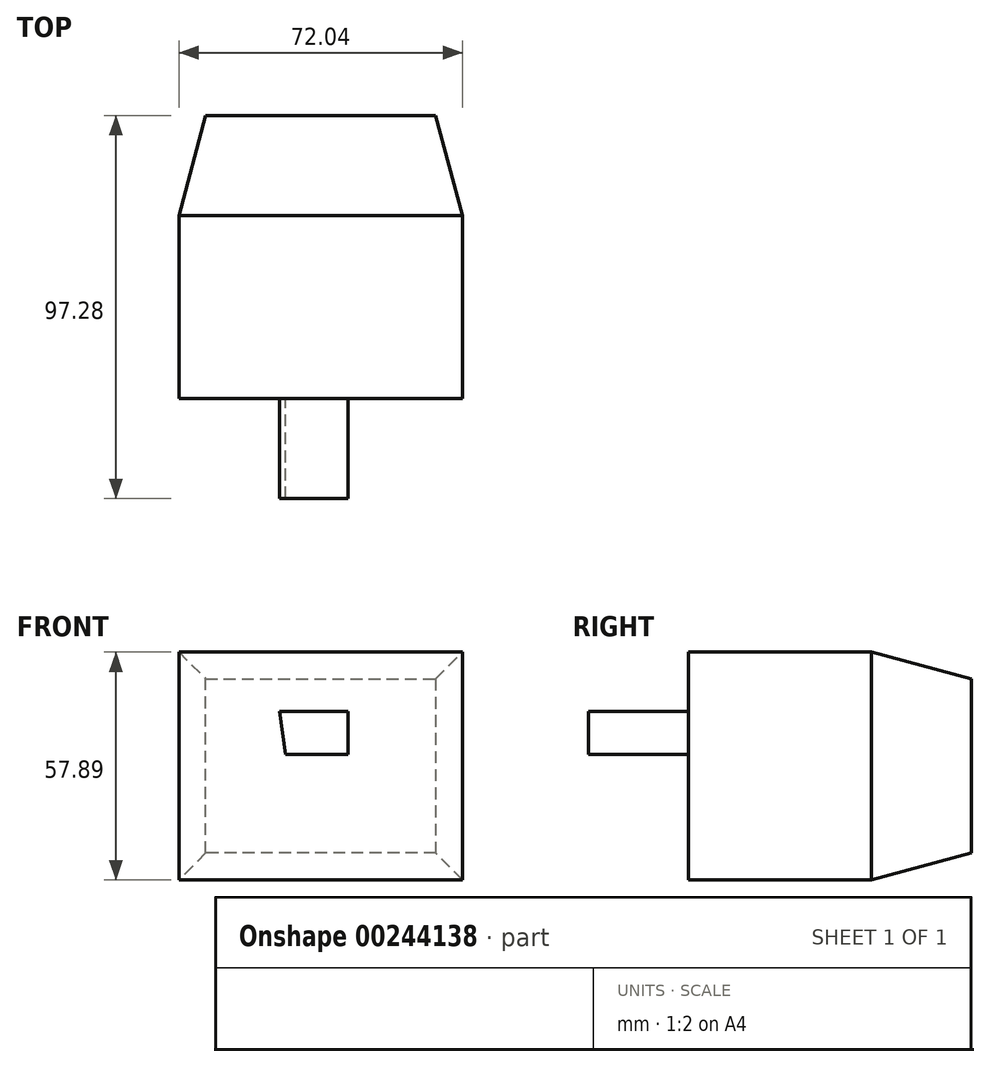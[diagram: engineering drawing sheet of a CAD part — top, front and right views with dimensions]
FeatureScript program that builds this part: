
annotation { "Feature Type Name" : "Feature", "Feature Type Description" : "" }
export const myFeature = defineFeature(function(context is Context, id is Id, definition is map)
    precondition{}
    {
        {
            var Q0;
            Q0=qCreatedBy(makeId("Front.planeOp"),FACE);
            var sketch = newSketch(context, id + "F0", { "sketchPlane" : qUnion([Q0])});
            skLineSegment(sketch, "E0.bottom", {"start": v(0, 0) * mm, "end": v(58.42, 0) * mm});
            skLineSegment(sketch, "E0.top", {"start": v(0, 44.27) * mm, "end": v(58.42, 44.27) * mm});
            skLineSegment(sketch, "E0.left", {"start": v(0, 0) * mm, "end": v(0, 44.27) * mm});
            skLineSegment(sketch, "E0.right", {"start": v(58.42, 0) * mm, "end": v(58.42, 44.27) * mm});
            skSolve(sketch);
        }
        {
            var Q0;
            Q0 = qSketchRegion(id + "F0", true);
            extrude(context, id + "F1", {"entities" : qUnion([Q0]), "depth" : 25.4 * mm, "hasDraft" : true, "draftAngle" : 15 * degree});
        }
        {
            var Q0;
            Q0=makeQuery(id+"F1.opExtrude","CAP_FACE",FACE,{"disambiguationData":[OSD([sQuery(id+"F0.wireOp",EDGE,"E0.bottom"),sQuery(id+"F0.wireOp",EDGE,"E0.top"),sQuery(id+"F0.wireOp",EDGE,"E0.left"),sQuery(id+"F0.wireOp",EDGE,"E0.right")])],"isStart":false});
            extrude(context, id + "F2", {"entities" : qUnion([Q0]), "operationType" : NewBodyOperationType.ADD, "depth" : 46.48 * mm, "offsetDistance" : 25.4 * mm});
        }
        {
            var Q0;
            Q0=makeQuery(id+"F2.opExtrude","CAP_FACE",FACE,{"disambiguationData":[OSD([sQuery(id+"F0.wireOp",EDGE,"E0.bottom"),sQuery(id+"F0.wireOp",EDGE,"E0.top"),sQuery(id+"F0.wireOp",EDGE,"E0.left"),sQuery(id+"F0.wireOp",EDGE,"E0.right")])],"isStart":false});
            var sketch = newSketch(context, id + "F3", { "sketchPlane" : qUnion([Q0])});
            skLineSegment(sketch, "E1", {"start": v(20.3, 25.1) * mm, "end": v(36.17, 25.1) * mm});
            skLineSegment(sketch, "E2", {"start": v(36.17, 25.1) * mm, "end": v(36.17, 36) * mm});
            skLineSegment(sketch, "E3", {"start": v(36.17, 36) * mm, "end": v(18.7, 36) * mm});
            skLineSegment(sketch, "E4", {"start": v(18.7, 36) * mm, "end": v(20.3, 25.1) * mm});
            skSolve(sketch);
        }
        {
            var Q0;
            Q0=makeQuery(id+"F3.imprint","IMPRINT",FACE,{"disambiguationData":[TD([[makeQuery(id+"F3.imprint","IMPRINT",EDGE,{"derivedFrom":sQuery(id+"F3.wireOp",EDGE,"E1")}),1.0]])]});
            extrude(context, id + "F4", {"entities" : qUnion([Q0]), "operationType" : NewBodyOperationType.ADD, "depth" : 25.4 * mm, "offsetDistance" : 25.4 * mm});
        }
    });
